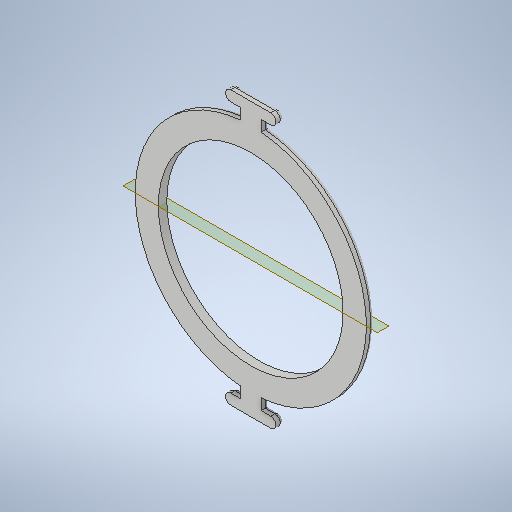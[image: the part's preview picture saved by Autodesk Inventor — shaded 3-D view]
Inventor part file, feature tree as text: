
AUTODESK INVENTOR PART (.ipt)
format: ipt  version: 2025 (Build 290162000, 162)  size: 1,363,968 bytes
history: native  units: mm
features: extrude x3, sketch x2, mirror x1, fillet x1, plane x1
ambient origin geometry x8: Origin, YZ Plane, XZ Plane, XY Plane, X Axis, Y Axis, Z Axis, Center Point
bodies: Volumenkörper1 (feature_tree)
feature tree (8):
  extrude  "Extrusion1"  Depth=87.92mm
  mirror  "Spiegeln1"
  fillet  "Rundung2"  Radius=10.0mm
  extrude  "Extrusion2"  Depth=2.5mm
  extrude  "Extrusion3"  Depth=5.0mm
  sketch  "Skizze1"  dims[d0=110.0mm d1=87.92mm d2=10.0mm]
  plane  "Arbeitsebene1"
  sketch  "Skizze3"  dims[d3=2.5mm d4=2.5mm d5=5.0mm d6=5.0mm d7=24.0mm d8=60.0mm d9=4.5mm d10=4.0mm d11=0.0mm d13=1.0mm d14=0.0mm d15=2.0mm d16=1.0mm d17=0.0mm]
